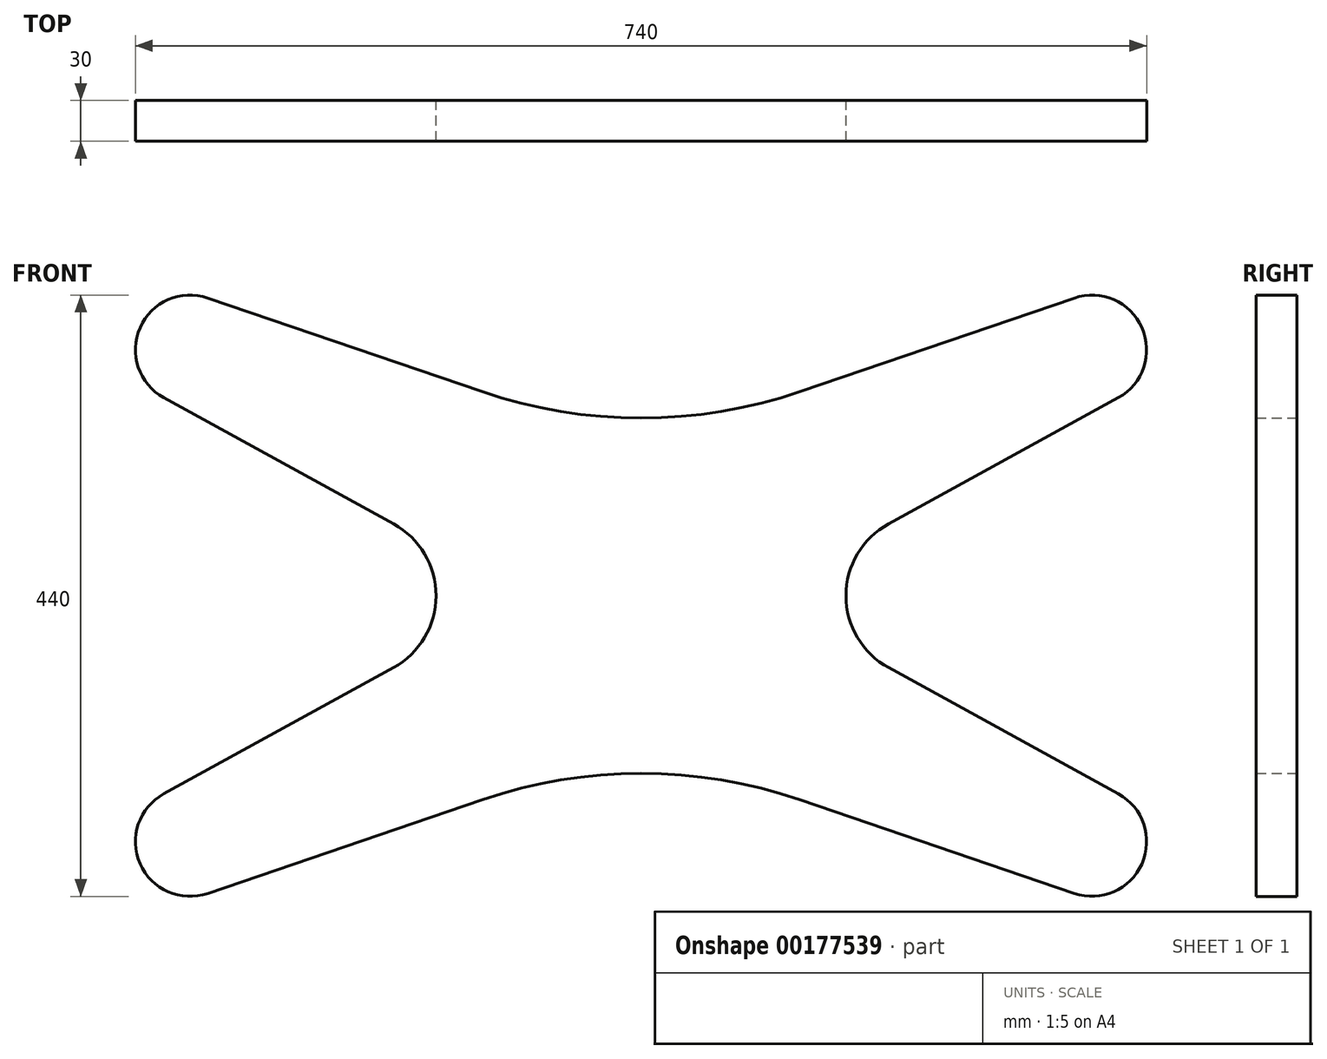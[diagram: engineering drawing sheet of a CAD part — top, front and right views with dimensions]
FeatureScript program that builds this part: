
annotation { "Feature Type Name" : "Feature", "Feature Type Description" : "" }
export const myFeature = defineFeature(function(context is Context, id is Id, definition is map)
    precondition{}
    {
        {
            var Q0;
            Q0=qCreatedBy(makeId("Front.planeOp"),FACE);
            var sketch = newSketch(context, id + "F0", { "sketchPlane" : qUnion([Q0])});
            skLineSegment(sketch, "E0", {"start": v(-317.08, 217.85) * mm, "end": v(-116.32, 149.31) * mm});
            skArc(sketch, "E1", {"start": v(-116.32, 149.31) * mm, "mid": v(-58.96, 134.86) * mm, "end": v(0, 130) * mm});
            skArc(sketch, "E2", {"start": v(-317.08, 217.85) * mm, "mid": v(-366.6, 196.15) * mm, "end": v(-349.26, 144.94) * mm});
            skLineSegment(sketch, "E3", {"start": v(-349.26, 144.94) * mm, "end": v(-181.12, 52.59) * mm});
            skArc(sketch, "E4", {"start": v(-150, 0) * mm, "mid": v(-158.36, 30.55) * mm, "end": v(-181.12, 52.59) * mm});
            skArc(sketch, "E5.MirrorCS", {"start": v(150, 0) * mm, "mid": v(158.36, 30.55) * mm, "end": v(181.12, 52.59) * mm});
            skLineSegment(sketch, "E6.MirrorCS", {"start": v(349.26, 144.94) * mm, "end": v(181.12, 52.59) * mm});
            skLineSegment(sketch, "E7.MirrorCS", {"start": v(317.08, 217.85) * mm, "end": v(116.32, 149.31) * mm});
            skArc(sketch, "E8.MirrorCS", {"start": v(317.08, 217.85) * mm, "mid": v(366.6, 196.15) * mm, "end": v(349.26, 144.94) * mm});
            skArc(sketch, "E9.MirrorCS", {"start": v(116.32, 149.31) * mm, "mid": v(58.96, 134.86) * mm, "end": v(0, 130) * mm});
            skArc(sketch, "E10.MirrorCS", {"start": v(150, 0) * mm, "mid": v(158.36, -30.55) * mm, "end": v(181.12, -52.59) * mm});
            skArc(sketch, "E11.MirrorCS", {"start": v(-150, 0) * mm, "mid": v(-158.36, -30.55) * mm, "end": v(-181.12, -52.59) * mm});
            skArc(sketch, "E12.MirrorCS", {"start": v(116.32, -149.31) * mm, "mid": v(58.96, -134.86) * mm, "end": v(0, -130) * mm});
            skArc(sketch, "E13.MirrorCS", {"start": v(317.08, -217.85) * mm, "mid": v(366.6, -196.15) * mm, "end": v(349.26, -144.94) * mm});
            skLineSegment(sketch, "E14.MirrorCS", {"start": v(317.08, -217.85) * mm, "end": v(116.32, -149.31) * mm});
            skLineSegment(sketch, "E15.MirrorCS", {"start": v(349.26, -144.94) * mm, "end": v(181.12, -52.59) * mm});
            skLineSegment(sketch, "E16.MirrorCS", {"start": v(-349.26, -144.94) * mm, "end": v(-181.12, -52.59) * mm});
            skLineSegment(sketch, "E17.MirrorCS", {"start": v(-317.08, -217.85) * mm, "end": v(-116.32, -149.31) * mm});
            skArc(sketch, "E18.MirrorCS", {"start": v(-116.32, -149.31) * mm, "mid": v(-58.96, -134.86) * mm, "end": v(0, -130) * mm});
            skArc(sketch, "E19.MirrorCS", {"start": v(-317.08, -217.85) * mm, "mid": v(-366.6, -196.15) * mm, "end": v(-349.26, -144.94) * mm});
            skSolve(sketch);
        }
        {
            var Q0;
            Q0=makeQuery(id+"F0.imprint","IMPRINT",FACE,{"disambiguationData":[TD([[makeQuery(id+"F0.imprint","IMPRINT",EDGE,{"derivedFrom":sQuery(id+"F0.wireOp",EDGE,"E0")}),-1.0]])]});
            extrude(context, id + "F1", {"entities" : qUnion([Q0]), "depth" : 30 * mm});
        }
    });
